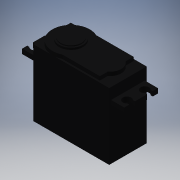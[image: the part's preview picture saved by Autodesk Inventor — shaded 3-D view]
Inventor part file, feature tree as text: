
AUTODESK INVENTOR PART (.ipt)
format: ipt  version: 2016 (Build 200138000, 138)  size: 151,552 bytes
history: native  units: in
note: dims shown in document units (in); Inventor stores cm internally (conversion verified against a paired STEP export)
features: mirror x1, other x1, sketch x1, imported_body x1
ambient origin geometry x8: Origin, YZ Plane, XZ Plane, XY Plane, X Axis, Y Axis, Z Axis, Center Point
bodies: Body1 (feature_tree)
feature tree (4):
  mirror  "Mirror2"
  other  "servo.ipt1"
  sketch  "Sketch3"
  imported_body  "Base1"
